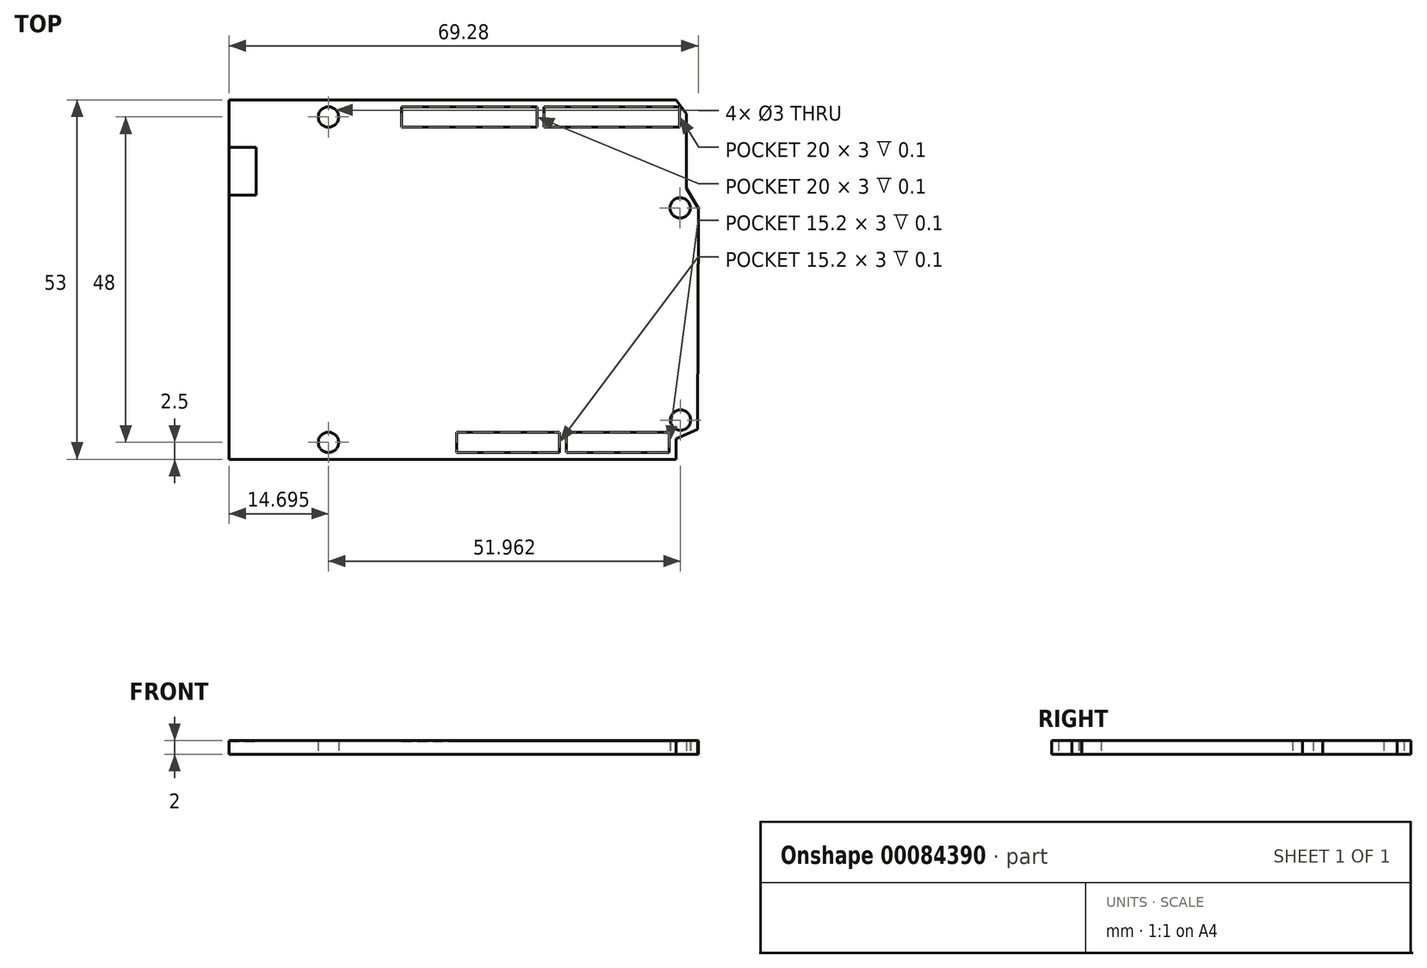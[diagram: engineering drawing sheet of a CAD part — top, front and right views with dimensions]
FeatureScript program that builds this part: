
annotation { "Feature Type Name" : "Feature", "Feature Type Description" : "" }
export const myFeature = defineFeature(function(context is Context, id is Id, definition is map)
    precondition{}
    {
        {
            var Q0;
            Q0=qCreatedBy(makeId("Top.planeOp"),FACE);
            var sketch = newSketch(context, id + "F0", { "sketchPlane" : qUnion([Q0])});
            skLineSegment(sketch, "E0.bottom", {"start": v(-33, 26.5) * mm, "end": v(33, 26.5) * mm});
            skLineSegment(sketch, "E0.top", {"start": v(-33, -26.5) * mm, "end": v(33, -26.5) * mm});
            skLineSegment(sketch, "E0.left", {"start": v(-33, 26.5) * mm, "end": v(-33, -26.5) * mm});
            skPoint(sketch, "E0.middle", {"position": v(0, 0) * mm});
            skLineSegment(sketch, "E1", {"start": v(33, 26.5) * mm, "end": v(34.5, 24.5) * mm});
            skLineSegment(sketch, "E2", {"start": v(34.5, 24.5) * mm, "end": v(34.5, 13.5) * mm});
            skLineSegment(sketch, "E3", {"start": v(33, -26.5) * mm, "end": v(33, -23.5) * mm});
            skLineSegment(sketch, "E4", {"start": v(33, -23.5) * mm, "end": v(36.2, -22.08) * mm});
            skLineSegment(sketch, "E5", {"start": v(34.5, 13.5) * mm, "end": v(36.28, 10.5) * mm});
            skLineSegment(sketch, "E6", {"start": v(36.28, 10.5) * mm, "end": v(36.2, -22.08) * mm});
            skCircle(sketch, "E7", {"center": v(33.66, -20.72) * mm, "radius": 1.5 * mm});
            skCircle(sketch, "E8", {"center": v(33.6, 10.58) * mm, "radius": 1.5 * mm});
            skLineSegment(sketch, "E9", {"start": v(-33, 26.5) * mm, "end": v(-20, 26.5) * mm});
            skCircle(sketch, "E10", {"center": v(-18.3, 24) * mm, "radius": 1.5 * mm});
            skLineSegment(sketch, "E11", {"start": v(-33, -26.5) * mm, "end": v(-20, -26.5) * mm});
            skCircle(sketch, "E12", {"center": v(-18.3, -24) * mm, "radius": 1.5 * mm});
            skLineSegment(sketch, "E13", {"start": v(-33, 26.5) * mm, "end": v(-33, 19.5) * mm});
            skLineSegment(sketch, "E14.bottom", {"start": v(-36, 19.5) * mm, "end": v(-29, 19.5) * mm});
            skLineSegment(sketch, "E14.top", {"start": v(-36, 12.5) * mm, "end": v(-29, 12.5) * mm});
            skLineSegment(sketch, "E14.left", {"start": v(-36, 19.5) * mm, "end": v(-36, 12.5) * mm});
            skLineSegment(sketch, "E14.right", {"start": v(-29, 19.5) * mm, "end": v(-29, 12.5) * mm});
            skSolve(sketch);
        }
        {
            var Q0;
            Q0=makeQuery(id+"F0.imprint","IMPRINT",FACE,{"disambiguationData":[TD([[makeQuery(id+"F0.imprint","IMPRINT",EDGE,{"derivedFrom":sQuery(id+"F0.wireOp",EDGE,"E0.bottom")}),-1.0]])]});
            extrude(context, id + "F1", {"entities" : qUnion([Q0]), "depth" : 2 * mm});
        }
        {
            var Q0;
            {var subQ5=sQuery(id+"F0.wireOp",EDGE,"E14.right");Q0=makeQuery(id+"F0.imprint","IMPRINT",FACE,{"disambiguationData":[TD([[makeQuery(id+"F0.imprint","IMPRINT",EDGE,{"derivedFrom":subQ5}),-1.0]])]});}
            extrude(context, id + "F2", {"entities" : qUnion([Q0]), "operationType" : NewBodyOperationType.REMOVE, "oppositeDirection" : true, "depth" : .1 * mm});
        }
        {
            var Q0;
            {var subQ5=sQuery(id+"F0.wireOp",EDGE,"E14.right");Q0=makeQuery(id+"F0.imprint","IMPRINT",FACE,{"disambiguationData":[TD([[makeQuery(id+"F0.imprint","IMPRINT",EDGE,{"derivedFrom":subQ5}),-1.0]])]});}
            extrude(context, id + "F3", {"entities" : qUnion([Q0]), "operationType" : NewBodyOperationType.ADD, "depth" : 1.9 * mm});
        }
        {
            var Q0;
            Q0=makeQuery(id+"F1.opExtrude","CAP_FACE",FACE,{"disambiguationData":[OSD([sQuery(id+"F0.wireOp",EDGE,"E0.bottom"),sQuery(id+"F0.wireOp",EDGE,"E0.top"),sQuery(id+"F0.wireOp",EDGE,"E0.left"),sQuery(id+"F0.wireOp",EDGE,"E1"),sQuery(id+"F0.wireOp",EDGE,"E2"),sQuery(id+"F0.wireOp",EDGE,"E3"),sQuery(id+"F0.wireOp",EDGE,"E4"),sQuery(id+"F0.wireOp",EDGE,"E5"),sQuery(id+"F0.wireOp",EDGE,"E6"),sQuery(id+"F0.wireOp",EDGE,"E7"),sQuery(id+"F0.wireOp",EDGE,"E8"),sQuery(id+"F0.wireOp",EDGE,"E9"),sQuery(id+"F0.wireOp",EDGE,"E10"),sQuery(id+"F0.wireOp",EDGE,"E11"),sQuery(id+"F0.wireOp",EDGE,"E12"),sQuery(id+"F0.wireOp",EDGE,"E13"),sQuery(id+"F0.wireOp",EDGE,"E14.bottom"),sQuery(id+"F0.wireOp",EDGE,"E14.top"),sQuery(id+"F0.wireOp",EDGE,"E14.right")])],"isStart":false});
            var sketch = newSketch(context, id + "F4", { "sketchPlane" : qUnion([Q0])});
            skLineSegment(sketch, "E15.bottom", {"start": v(13.5, 25.5) * mm, "end": v(33.5, 25.5) * mm});
            skLineSegment(sketch, "E15.top", {"start": v(13.5, 22.5) * mm, "end": v(33.5, 22.5) * mm});
            skLineSegment(sketch, "E15.left", {"start": v(13.5, 25.5) * mm, "end": v(13.5, 22.5) * mm});
            skLineSegment(sketch, "E15.right", {"start": v(33.5, 25.5) * mm, "end": v(33.5, 22.5) * mm});
            skLineSegment(sketch, "E16.bottom", {"start": v(-7.5, 25.5) * mm, "end": v(12.5, 25.5) * mm});
            skLineSegment(sketch, "E16.top", {"start": v(-7.5, 22.5) * mm, "end": v(12.5, 22.5) * mm});
            skLineSegment(sketch, "E16.left", {"start": v(-7.5, 25.5) * mm, "end": v(-7.5, 22.5) * mm});
            skLineSegment(sketch, "E16.right", {"start": v(12.5, 25.5) * mm, "end": v(12.5, 22.5) * mm});
            skLineSegment(sketch, "E17.bottom", {"start": v(0.6, -22.5) * mm, "end": v(15.8, -22.5) * mm});
            skLineSegment(sketch, "E17.top", {"start": v(0.6, -25.5) * mm, "end": v(15.8, -25.5) * mm});
            skLineSegment(sketch, "E17.left", {"start": v(0.6, -22.5) * mm, "end": v(0.6, -25.5) * mm});
            skLineSegment(sketch, "E17.right", {"start": v(15.8, -22.5) * mm, "end": v(15.8, -25.5) * mm});
            skLineSegment(sketch, "E18.bottom", {"start": v(16.8, -22.5) * mm, "end": v(32, -22.5) * mm});
            skLineSegment(sketch, "E18.top", {"start": v(16.8, -25.5) * mm, "end": v(32, -25.5) * mm});
            skLineSegment(sketch, "E18.left", {"start": v(16.8, -22.5) * mm, "end": v(16.8, -25.5) * mm});
            skLineSegment(sketch, "E18.right", {"start": v(32, -22.5) * mm, "end": v(32, -25.5) * mm});
            skSolve(sketch);
        }
        {
            var Q0;
            Q0=makeQuery(id+"F4.imprint","IMPRINT",FACE,{"disambiguationData":[TD([[makeQuery(id+"F4.imprint","IMPRINT",EDGE,{"derivedFrom":sQuery(id+"F4.wireOp",EDGE,"E16.bottom")}),-1.0]])]});
            var Q1;
            Q1=makeQuery(id+"F4.imprint","IMPRINT",FACE,{"disambiguationData":[TD([[makeQuery(id+"F4.imprint","IMPRINT",EDGE,{"derivedFrom":sQuery(id+"F4.wireOp",EDGE,"E15.bottom")}),-1.0]])]});
            extrude(context, id + "F5", {"entities" : qUnion([Q0, Q1]), "operationType" : NewBodyOperationType.REMOVE, "oppositeDirection" : true, "depth" : .1 * mm});
        }
        {
            var Q0;
            Q0=makeQuery(id+"F4.imprint","IMPRINT",FACE,{"disambiguationData":[TD([[makeQuery(id+"F4.imprint","IMPRINT",EDGE,{"derivedFrom":sQuery(id+"F4.wireOp",EDGE,"E17.bottom")}),-1.0]])]});
            var Q1;
            Q1=makeQuery(id+"F4.imprint","IMPRINT",FACE,{"disambiguationData":[TD([[makeQuery(id+"F4.imprint","IMPRINT",EDGE,{"derivedFrom":sQuery(id+"F4.wireOp",EDGE,"E18.bottom")}),-1.0]])]});
            extrude(context, id + "F6", {"entities" : qUnion([Q0, Q1]), "operationType" : NewBodyOperationType.REMOVE, "oppositeDirection" : true, "depth" : .1 * mm});
        }
    });
